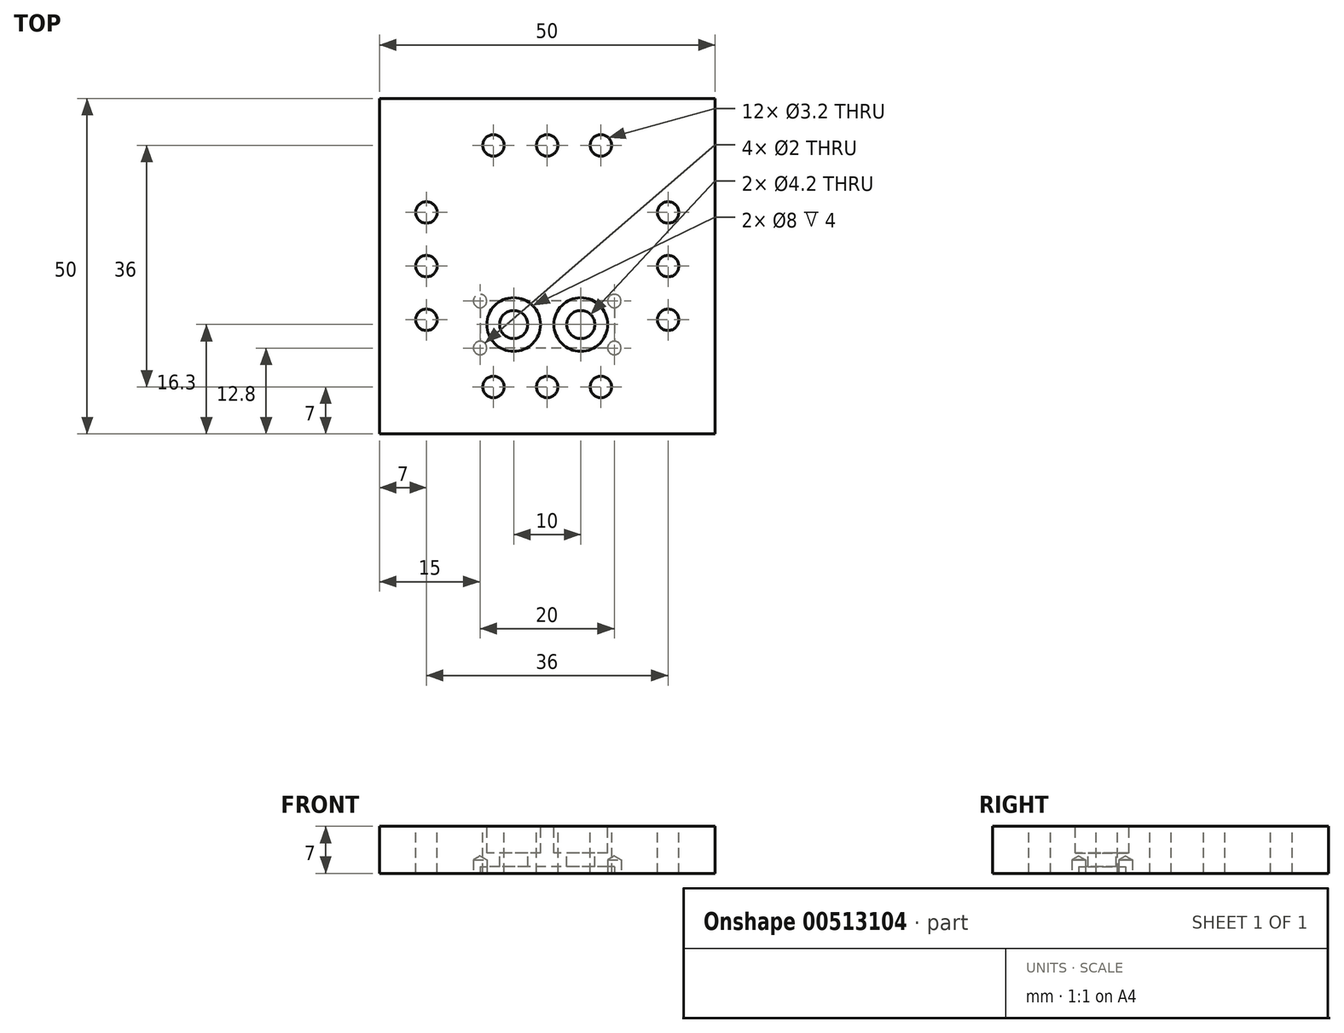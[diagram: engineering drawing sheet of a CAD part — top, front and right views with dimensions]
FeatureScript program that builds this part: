
annotation { "Feature Type Name" : "Feature", "Feature Type Description" : "" }
export const myFeature = defineFeature(function(context is Context, id is Id, definition is map)
    precondition{}
    {
        {
            var Q0;
            Q0=qCreatedBy(makeId("Top.planeOp"),FACE);
            var sketch = newSketch(context, id + "F0", { "sketchPlane" : qUnion([Q0])});
            skLineSegment(sketch, "E0.bottom", {"start": v(25, 25) * mm, "end": v(-25, 25) * mm});
            skLineSegment(sketch, "E0.top", {"start": v(25, -25) * mm, "end": v(-25, -25) * mm});
            skLineSegment(sketch, "E0.left", {"start": v(25, 25) * mm, "end": v(25, -25) * mm});
            skLineSegment(sketch, "E0.right", {"start": v(-25, 25) * mm, "end": v(-25, -25) * mm});
            skPoint(sketch, "E0.middle", {"position": v(0, 0) * mm});
            skSolve(sketch);
        }
        {
            var Q0;
            Q0 = qSketchRegion(id + "F0", true);
            extrude(context, id + "F1", {"entities" : qUnion([Q0]), "depth" : 7 * mm, "offsetDistance" : 25 * mm});
        }
        {
            var Q0;
            Q0=makeQuery(id+"F1.opExtrude","CAP_FACE",FACE,{"disambiguationData":[OSD([sQuery(id+"F0.wireOp",EDGE,"E0.bottom"),sQuery(id+"F0.wireOp",EDGE,"E0.top"),sQuery(id+"F0.wireOp",EDGE,"E0.left"),sQuery(id+"F0.wireOp",EDGE,"E0.right")])],"isStart":false});
            var sketch = newSketch(context, id + "F2", { "sketchPlane" : qUnion([Q0])});
            skPoint(sketch, "E1", {"position": v(0, 0) * mm});
            skPoint(sketch, "E2", {"position": v(0, -18) * mm});
            skPoint(sketch, "E3", {"position": v(-8, -18) * mm});
            skPoint(sketch, "E4", {"position": v(8, -18) * mm});
            skLineSegment(sketch, "E5", {"start": v(0, 0) * mm, "end": v(-18, 0) * mm});
            skLineSegment(sketch, "E6", {"start": v(0, 0) * mm, "end": v(18, 0) * mm});
            skPoint(sketch, "E7", {"position": v(-18, 0) * mm});
            skPoint(sketch, "E8", {"position": v(18, 0) * mm});
            skPoint(sketch, "E9", {"position": v(-18, -8) * mm});
            skPoint(sketch, "E10", {"position": v(-18, 8) * mm});
            skPoint(sketch, "E11", {"position": v(18, -8) * mm});
            skPoint(sketch, "E12", {"position": v(18, 8) * mm});
            skPoint(sketch, "E13", {"position": v(0, 18) * mm});
            skPoint(sketch, "E14", {"position": v(-8, 18) * mm});
            skPoint(sketch, "E15", {"position": v(8, 18) * mm});
            skLineSegment(sketch, "E16", {"start": v(-5, -8.7) * mm, "end": v(5, -8.7) * mm});
            skPoint(sketch, "E17", {"position": v(0, -12.2) * mm});
            skSolve(sketch);
        }
        {
            var Q0;
            Q0=sQuery(id+"F2.wireOp",VERTEX,"E10");
            var Q1;
            Q1=sQuery(id+"F2.wireOp",VERTEX,"E7");
            var Q2;
            Q2=sQuery(id+"F2.wireOp",VERTEX,"E9");
            var Q3;
            Q3=sQuery(id+"F2.wireOp",VERTEX,"E3");
            var Q4;
            Q4=sQuery(id+"F2.wireOp",VERTEX,"E2");
            var Q5;
            Q5=sQuery(id+"F2.wireOp",VERTEX,"E4");
            var Q6;
            Q6=sQuery(id+"F2.wireOp",VERTEX,"E11");
            var Q7;
            Q7=sQuery(id+"F2.wireOp",VERTEX,"E8");
            var Q8;
            Q8=sQuery(id+"F2.wireOp",VERTEX,"E12");
            var Q9;
            Q9=sQuery(id+"F2.wireOp",VERTEX,"E14");
            var Q10;
            Q10=sQuery(id+"F2.wireOp",VERTEX,"E13");
            var Q11;
            Q11=sQuery(id+"F2.wireOp",VERTEX,"E15");
            var Q12;
            Q12=makeQuery(id+"F1.opExtrude","SWEPT_BODY",BODY,{"disambiguationData":[OSD([sQuery(id+"F0.wireOp",EDGE,"E0.bottom"),sQuery(id+"F0.wireOp",EDGE,"E0.top"),sQuery(id+"F0.wireOp",EDGE,"E0.left"),sQuery(id+"F0.wireOp",EDGE,"E0.right")])]});
            hole(context, id + "F3", {"style" : HoleStyle.SIMPLE, "endStyle" : HoleEndStyle.THROUGH, "holeDiameter" : 3.2 * mm, "isTappedThrough" : true, "tappedDepth" : 12 * mm, "tapClearance" : 3, "locations" : qUnion([Q0, Q1, Q2, Q3, Q4, Q5, Q6, Q7, Q8, Q9, Q10, Q11]), "scope" : qUnion([Q12])});
        }
        {
            var Q0;
            Q0=sQuery(id+"F2.wireOp",VERTEX,"E16.start");
            var Q1;
            Q1=sQuery(id+"F2.wireOp",VERTEX,"E16.end");
            var Q2;
            Q2=makeQuery(id+"F1.opExtrude","SWEPT_BODY",BODY,{"disambiguationData":[OSD([sQuery(id+"F0.wireOp",EDGE,"E0.bottom"),sQuery(id+"F0.wireOp",EDGE,"E0.top"),sQuery(id+"F0.wireOp",EDGE,"E0.left"),sQuery(id+"F0.wireOp",EDGE,"E0.right")])]});
            hole(context, id + "F4", {"style" : HoleStyle.C_BORE, "endStyle" : HoleEndStyle.THROUGH, "holeDiameter" : 4.2 * mm, "cBoreDiameter" : 8 * mm, "cBoreDepth" : 4 * mm, "isTappedThrough" : true, "tappedDepth" : 12 * mm, "tapClearance" : 3, "locations" : qUnion([Q0, Q1]), "scope" : qUnion([Q2])});
        }
        {
            var Q0;
            Q0=makeQuery(id+"F1.opExtrude","CAP_FACE",FACE,{"disambiguationData":[OSD([sQuery(id+"F0.wireOp",EDGE,"E0.bottom"),sQuery(id+"F0.wireOp",EDGE,"E0.top"),sQuery(id+"F0.wireOp",EDGE,"E0.left"),sQuery(id+"F0.wireOp",EDGE,"E0.right")])],"isStart":true});
            var sketch = newSketch(context, id + "F5", { "sketchPlane" : qUnion([Q0])});
            skPoint(sketch, "E18.middle", {"position": v(0, 0) * mm});
            skLineSegment(sketch, "E19.bottom", {"start": v(10, 5.2) * mm, "end": v(-10, 5.2) * mm});
            skLineSegment(sketch, "E19.top", {"start": v(10, 12.2) * mm, "end": v(-10, 12.2) * mm});
            skLineSegment(sketch, "E19.left", {"start": v(10, 5.2) * mm, "end": v(10, 12.2) * mm});
            skLineSegment(sketch, "E19.right", {"start": v(-10, 5.2) * mm, "end": v(-10, 12.2) * mm});
            skPoint(sketch, "E19.middle", {"position": v(0, 8.7) * mm});
            skSolve(sketch);
        }
        {
            var Q0;
            Q0=makeQuery(id+"F5.imprint","IMPRINT",FACE,{"disambiguationData":[TD([[makeQuery(id+"F5.imprint","IMPRINT",EDGE,{"derivedFrom":sQuery(id+"F5.wireOp",EDGE,"E19.bottom")}),-1.0]])]});
            extrude(context, id + "F6", {"entities" : qUnion([Q0]), "operationType" : NewBodyOperationType.REMOVE, "oppositeDirection" : true, "depth" : 1 * mm, "offsetDistance" : 25 * mm});
        }
        {
            var Q0;
            Q0=sQuery(id+"F5.wireOp",VERTEX,"E19.right.start");
            var Q1;
            Q1=sQuery(id+"F5.wireOp",VERTEX,"E19.top.end");
            var Q2;
            Q2=sQuery(id+"F5.wireOp",VERTEX,"E19.left.end");
            var Q3;
            Q3=sQuery(id+"F5.wireOp",VERTEX,"E19.left.start");
            var Q4;
            Q4=makeQuery(id+"F1.opExtrude","SWEPT_BODY",BODY,{"disambiguationData":[OSD([sQuery(id+"F0.wireOp",EDGE,"E0.bottom"),sQuery(id+"F0.wireOp",EDGE,"E0.top"),sQuery(id+"F0.wireOp",EDGE,"E0.left"),sQuery(id+"F0.wireOp",EDGE,"E0.right")])]});
            hole(context, id + "F7", {"style" : HoleStyle.SIMPLE, "endStyle" : HoleEndStyle.BLIND, "holeDiameter" : 2 * mm, "holeDepth" : 1 * mm, "isTappedThrough" : true, "tappedDepth" : 12 * mm, "tapClearance" : 3, "locations" : qUnion([Q0, Q1, Q2, Q3]), "scope" : qUnion([Q4])});
        }
    });
